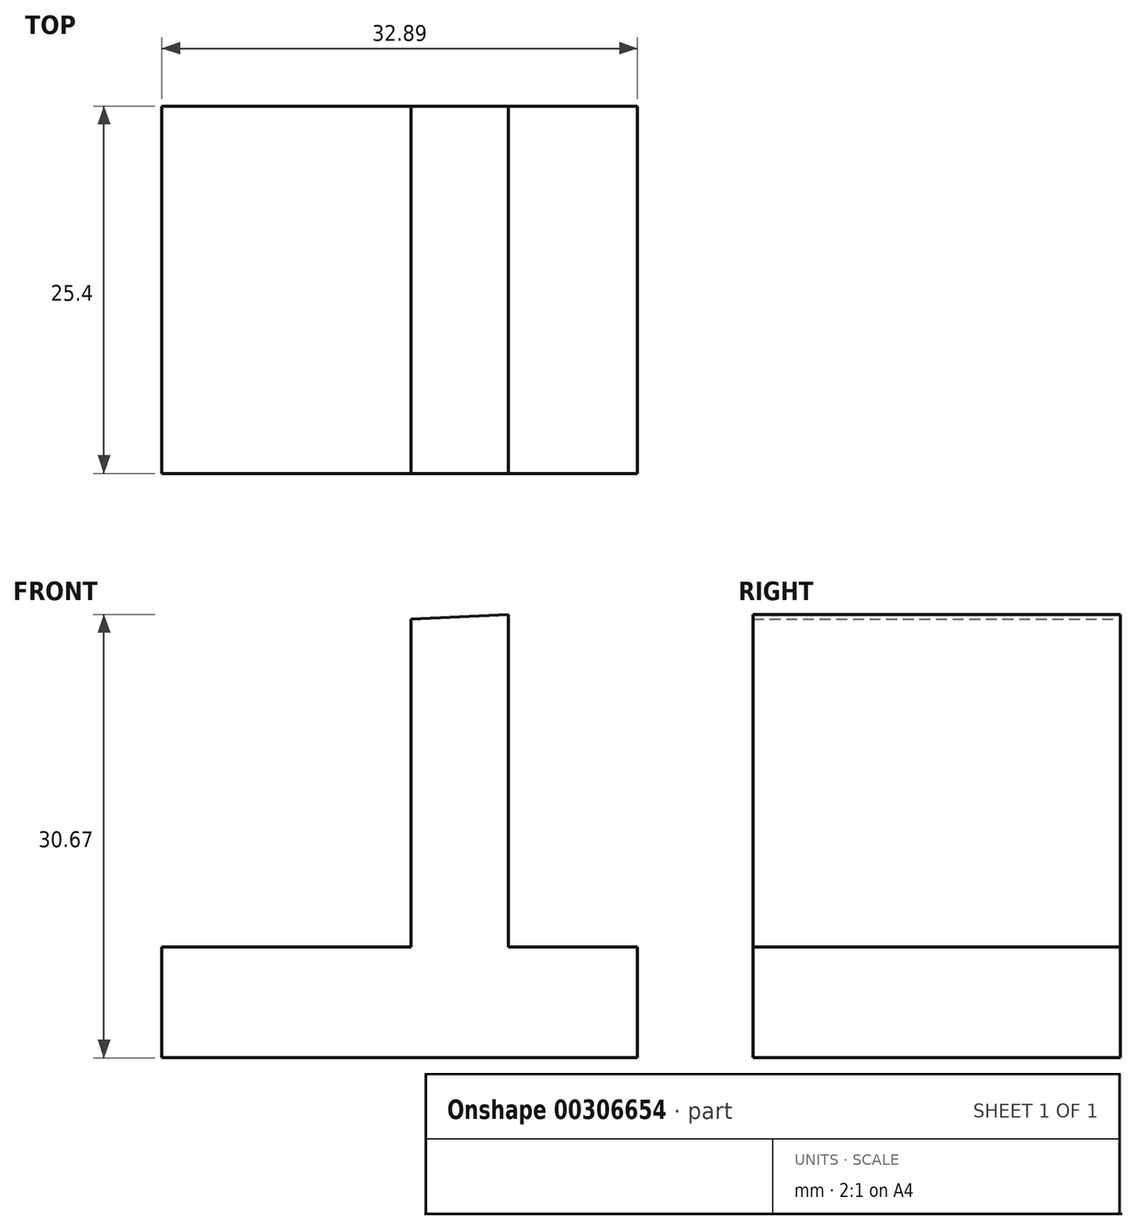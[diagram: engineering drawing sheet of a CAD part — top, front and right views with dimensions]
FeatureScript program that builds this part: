
annotation { "Feature Type Name" : "Feature", "Feature Type Description" : "" }
export const myFeature = defineFeature(function(context is Context, id is Id, definition is map)
    precondition{}
    {
        {
            var Q0;
            Q0=qCreatedBy(makeId("Front.planeOp"),FACE);
            var sketch = newSketch(context, id + "F0", { "sketchPlane" : qUnion([Q0])});
            skLineSegment(sketch, "E0", {"start": v(-55.58, 44.24) * mm, "end": v(-55.58, 21.56) * mm});
            skLineSegment(sketch, "E1", {"start": v(-55.58, 21.56) * mm, "end": v(-72.82, 21.56) * mm});
            skLineSegment(sketch, "E2", {"start": v(-72.82, 21.56) * mm, "end": v(-72.82, 13.9) * mm});
            skLineSegment(sketch, "E3", {"start": v(-72.82, 13.9) * mm, "end": v(-39.93, 13.9) * mm});
            skLineSegment(sketch, "E4", {"start": v(-39.93, 13.9) * mm, "end": v(-39.93, 21.56) * mm});
            skLineSegment(sketch, "E5", {"start": v(-39.93, 21.56) * mm, "end": v(-48.87, 21.56) * mm});
            skLineSegment(sketch, "E6", {"start": v(-48.87, 21.56) * mm, "end": v(-48.87, 44.56) * mm});
            skLineSegment(sketch, "E7", {"start": v(-48.87, 44.56) * mm, "end": v(-55.58, 44.24) * mm});
            skSolve(sketch);
        }
        {
            var Q0;
            Q0 = qSketchRegion(id + "F0", true);
            extrude(context, id + "F1", {"entities" : qUnion([Q0]), "depth" : 25.4 * mm});
        }
    });
